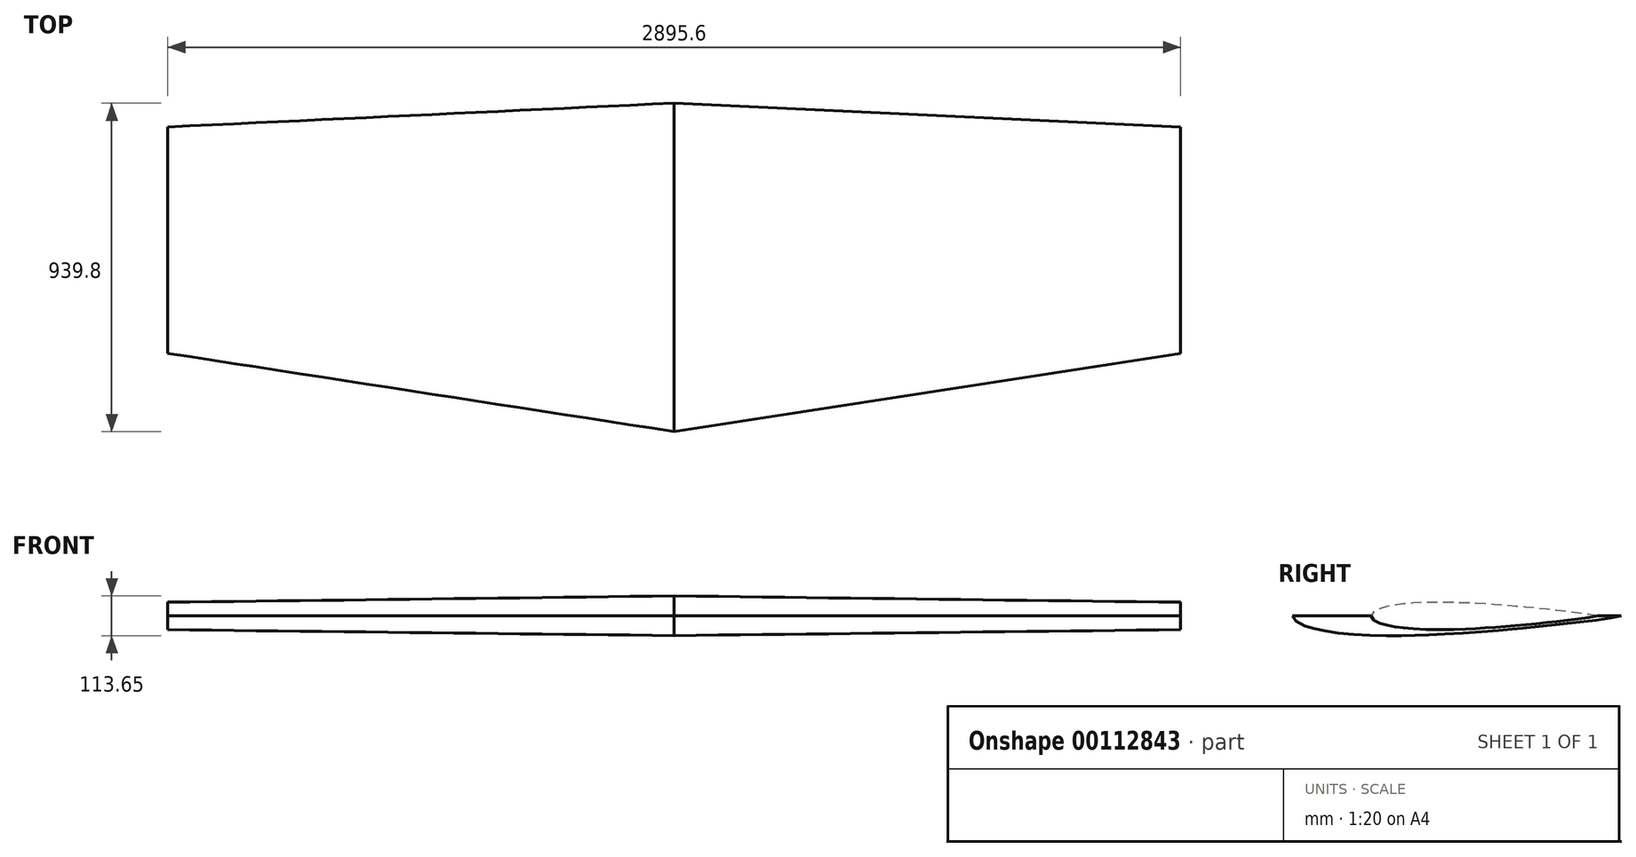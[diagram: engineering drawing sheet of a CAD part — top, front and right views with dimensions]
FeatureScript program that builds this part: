
annotation { "Feature Type Name" : "Feature", "Feature Type Description" : "" }
export const myFeature = defineFeature(function(context is Context, id is Id, definition is map)
    precondition{}
    {
        {
            var Q0;
            Q0=qCreatedBy(makeId("Right.planeOp"),FACE);
            var sketch = newSketch(context, id + "F0", { "sketchPlane" : qUnion([Q0])});
            skPoint(sketch, "E0", {"position": v(-249.42, 0.74) * mm});
            skLineSegment(sketch, "E1", {"start": v(-249.42, 0.74) * mm, "end": v(690.38, 0) * mm, "construction": true});
            skFitSpline(sketch, "E2", {"points": [v(-249.42, 0.74) * mm, v(-243.69, 12.5) * mm, v(-218.28, 28.3) * mm, v(-181.92, 39.25) * mm, v(-137.9, 47.4) * mm, v(-59, 54.6) * mm, v(32.62, 57.29) * mm, v(100.38, 56.56) * mm, v(172.6, 53.47) * mm, v(289.07, 45.9) * mm, v(371.83, 38.86) * mm, v(414.94, 34.74) * mm, v(545.47, 20.66) * mm, v(641.98, 8.53) * mm, v(690.38, 0) * mm], "startDerivative": vector(8.38, 483.2) * mm, "endDerivative": vector(722.08, -137.17) * mm});
            skFitSpline(sketch, "E3.MirrorCS", {"points": [v(-249.42, 0.74) * mm, v(-243.7, -11.04) * mm, v(-218.32, -26.88) * mm, v(-181.98, -37.88) * mm, v(-137.98, -46.1) * mm, v(-59.08, -53.44) * mm, v(32.53, -56.26) * mm, v(100.3, -55.63) * mm, v(172.52, -52.66) * mm, v(289, -45.27) * mm, v(371.77, -38.36) * mm, v(414.88, -34.3) * mm, v(545.43, -20.43) * mm, v(641.97, -8.45) * mm, v(690.38, 0) * mm], "startDerivative": vector(7.62, -483.2) * mm, "endDerivative": vector(722.3, 136.04) * mm});
            skSolve(sketch);
        }
        {
            var Q0;
            Q0=qCreatedBy(makeId("Top.planeOp"),FACE);
            var sketch = newSketch(context, id + "F1", { "sketchPlane" : qUnion([Q0])});
            skPoint(sketch, "E4.0", {"position": v(0, -249.42) * mm});
            skPoint(sketch, "E4.1", {"position": v(0, 690.38) * mm});
            skLineSegment(sketch, "E5", {"start": v(0, -249.42) * mm, "end": v(1447.8, -25.14) * mm});
            skLineSegment(sketch, "E6", {"start": v(1447.8, -25.14) * mm, "end": v(1447.8, 621.63) * mm});
            skLineSegment(sketch, "E7", {"start": v(1447.8, 621.63) * mm, "end": v(0, 690.38) * mm});
            skLineSegment(sketch, "E8", {"start": v(0, 690.38) * mm, "end": v(0, -249.42) * mm});
            skSolve(sketch);
        }
        {
            var Q0;
            Q0=qCreatedBy(makeId("Right.planeOp"),FACE);
            cPlane(context, id + "F2", {"entities" : qUnion([Q0]), "cplaneType" : CPlaneType.OFFSET, "offset" : 1447.8 * mm, "width" : 152.4 * mm, "height" : 152.4 * mm});
        }
        {
            var Q0;
            Q0=qCreatedBy(id+"F2.planeOp",FACE);
            var sketch = newSketch(context, id + "F3", { "sketchPlane" : qUnion([Q0])});
            skPoint(sketch, "E9", {"position": v(-25.14, 0) * mm});
            skLineSegment(sketch, "E10", {"start": v(-25.14, 0) * mm, "end": v(622.56, 0) * mm, "construction": true});
            skPoint(sketch, "E11.1", {"position": v(621.63, 0) * mm});
            skFitSpline(sketch, "E12", {"points": [v(-25.14, 0) * mm, v(-20.24, 9.38) * mm, v(-3.9, 19.1) * mm, v(21.22, 26.62) * mm, v(51.18, 31.97) * mm, v(86.98, 36.15) * mm, v(169.43, 39.2) * mm, v(243.4, 37.2) * mm, v(287.28, 35.26) * mm, v(333.42, 31.92) * mm, v(380.27, 28.22) * mm, v(429.25, 23.87) * mm, v(478, 18.7) * mm, v(528.82, 13.2) * mm, v(581.9, 6.37) * mm, v(622.56, 0) * mm], "startDerivative": vector(10.22, 305.3) * mm, "endDerivative": vector(602.76, -103.53) * mm});
            skFitSpline(sketch, "E13.MirrorCS", {"points": [v(-25.14, 0) * mm, v(-20.24, -9.38) * mm, v(-3.9, -19.1) * mm, v(21.22, -26.62) * mm, v(51.18, -31.97) * mm, v(86.98, -36.15) * mm, v(169.43, -39.2) * mm, v(243.4, -37.2) * mm, v(287.28, -35.26) * mm, v(333.42, -31.92) * mm, v(380.27, -28.22) * mm, v(429.25, -23.87) * mm, v(478, -18.7) * mm, v(528.82, -13.2) * mm, v(581.9, -6.37) * mm, v(622.56, 0) * mm], "startDerivative": vector(10.22, -305.3) * mm, "endDerivative": vector(602.76, 103.53) * mm});
            skSolve(sketch);
        }
        {
            var Q0;
            Q0=makeQuery(id+"F0.imprint","IMPRINT",FACE,{"disambiguationData":[TD([[makeQuery(id+"F0.imprint","IMPRINT",EDGE,{"derivedFrom":sQuery(id+"F0.wireOp",EDGE,"E2")}),-1.0]])]});
            var Q1;
            Q1=makeQuery(id+"F3.imprint","IMPRINT",FACE,{"disambiguationData":[TD([[makeQuery(id+"F3.imprint","IMPRINT",EDGE,{"derivedFrom":sQuery(id+"F3.wireOp",EDGE,"E12")}),-1.0]])]});
            loft(context, id + "F4", {"sheetProfilesArray" : [{ "sheetProfileEntities" : qUnion([Q0]) }, { "sheetProfileEntities" : qUnion([Q1]) }]});
        }
        {
            var Q0;
            Q0=makeQuery(id+"F4.opLoft","SWEPT_BODY",BODY,{"disambiguationData":[OSD([makeQuery(id+"F0.imprint","IMPRINT",FACE,{"disambiguationData":[TD([[makeQuery(id+"F0.imprint","IMPRINT",EDGE,{"derivedFrom":sQuery(id+"F0.wireOp",EDGE,"E2")}),-1.0]])]}),makeQuery(id+"F3.imprint","IMPRINT",FACE,{"disambiguationData":[TD([[makeQuery(id+"F3.imprint","IMPRINT",EDGE,{"derivedFrom":sQuery(id+"F3.wireOp",EDGE,"E12")}),-1.0]])]})])]});
            var Q1;
            Q1=qCreatedBy(makeId("Right.planeOp"),FACE);
            mirror(context, id + "F5", {"operationType" : NewBodyOperationType.ADD, "entities" : qUnion([Q0]), "mirrorPlane" : qUnion([Q1])});
        }
    });
